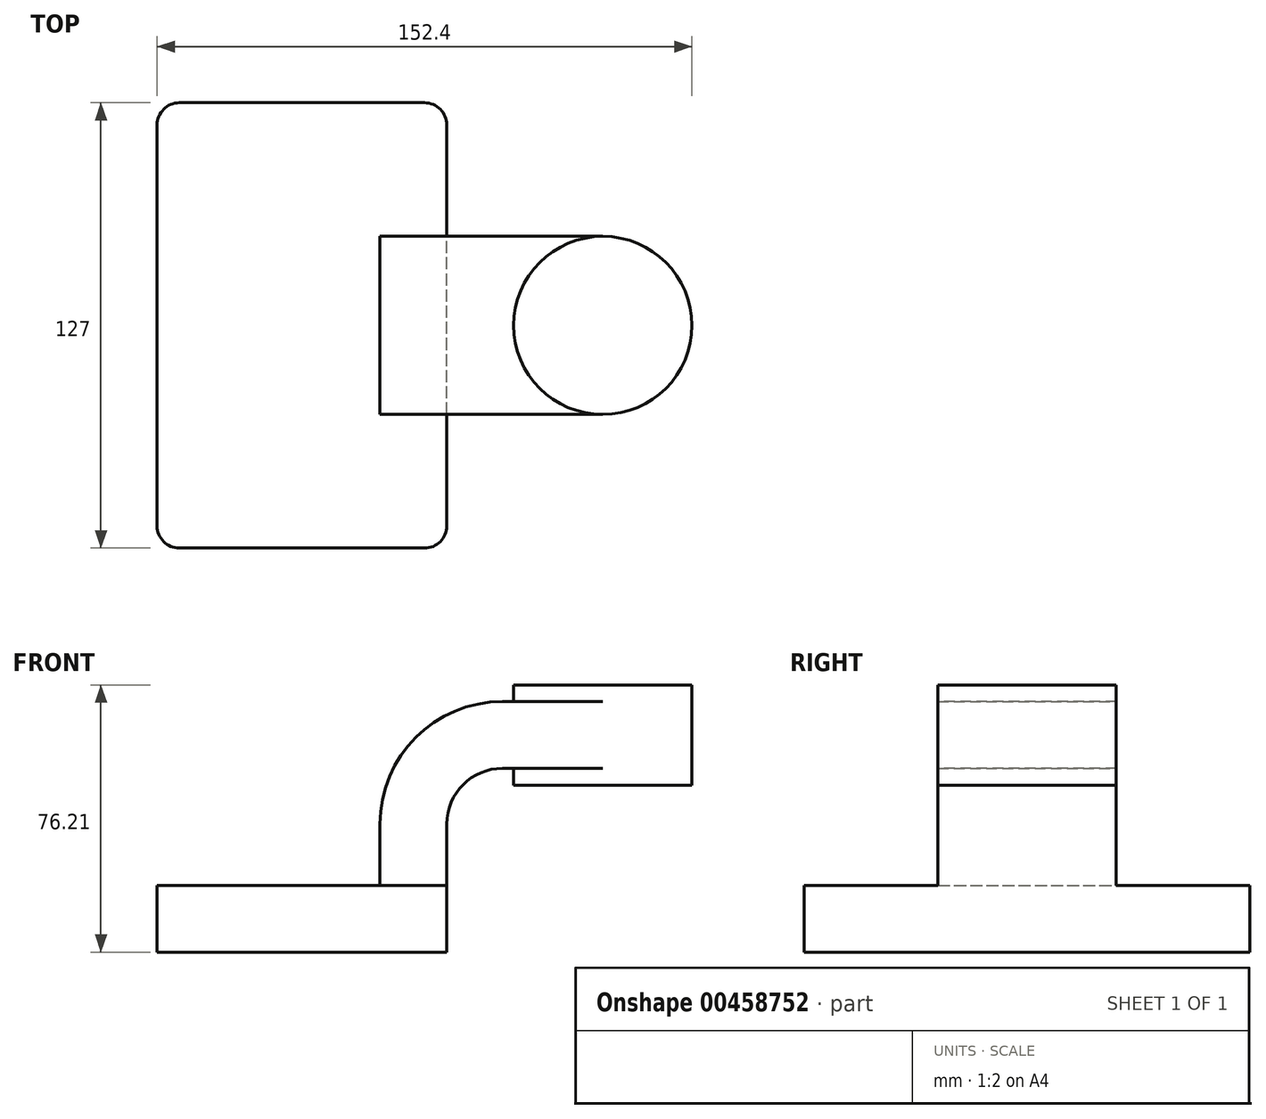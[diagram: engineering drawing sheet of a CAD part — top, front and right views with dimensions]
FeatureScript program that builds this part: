
annotation { "Feature Type Name" : "Feature", "Feature Type Description" : "" }
export const myFeature = defineFeature(function(context is Context, id is Id, definition is map)
    precondition{}
    {
        {
            var Q0;
            Q0=qCreatedBy(makeId("Front.planeOp"),FACE);
            var sketch = newSketch(context, id + "F0", { "sketchPlane" : qUnion([Q0])});
            skLineSegment(sketch, "E0.bottom", {"start": v(41.28, -9.52) * mm, "end": v(-41.28, -9.53) * mm});
            skLineSegment(sketch, "E0.top", {"start": v(41.28, 9.53) * mm, "end": v(-41.28, 9.52) * mm});
            skLineSegment(sketch, "E0.left", {"start": v(41.28, -9.52) * mm, "end": v(41.28, 9.53) * mm});
            skLineSegment(sketch, "E0.right", {"start": v(-41.28, -9.53) * mm, "end": v(-41.28, 9.52) * mm});
            skPoint(sketch, "E0.middle", {"position": v(0, 0) * mm});
            skLineSegment(sketch, "E1.bottom", {"start": v(111.12, 38.1) * mm, "end": v(60.32, 38.1) * mm});
            skLineSegment(sketch, "E1.top", {"start": v(111.12, 66.68) * mm, "end": v(60.32, 66.68) * mm});
            skLineSegment(sketch, "E1.left", {"start": v(111.12, 38.1) * mm, "end": v(111.12, 66.68) * mm});
            skLineSegment(sketch, "E1.right", {"start": v(60.32, 38.1) * mm, "end": v(60.32, 66.68) * mm});
            skPoint(sketch, "E1.middle", {"position": v(85.72, 52.39) * mm});
            skLineSegment(sketch, "E2", {"start": v(41.28, 9.53) * mm, "end": v(41.28, 27) * mm});
            skArc(sketch, "E3", {"start": v(41.28, 27) * mm, "mid": v(45.92, 38.23) * mm, "end": v(57.15, 42.88) * mm});
            skLineSegment(sketch, "E4", {"start": v(57.15, 42.88) * mm, "end": v(85.72, 42.88) * mm});
            skLineSegment(sketch, "E5.0", {"start": v(57.15, 61.93) * mm, "end": v(85.72, 61.93) * mm});
            skArc(sketch, "E5.1", {"start": v(22.23, 27) * mm, "mid": v(32.45, 51.7) * mm, "end": v(57.15, 61.93) * mm});
            skLineSegment(sketch, "E5.2", {"start": v(22.23, 9.53) * mm, "end": v(22.23, 27) * mm});
            skFitSpline(sketch, "E6", {"points": [v(-41.28, 9.52) * mm, v(57.15, 61.93) * mm], "startDerivative": vector(-5.75, 89.36) * mm, "endDerivative": vector(123.9, -8.8) * mm});
            skLineSegment(sketch, "E7", {"start": v(85.72, 66.68) * mm, "end": v(85.72, 38.1) * mm});
            skSolve(sketch);
        }
        {
            var Q0;
            Q0=makeQuery(id+"F0.imprint","IMPRINT",FACE,{"disambiguationData":[TD([[makeQuery(id+"F0.imprint","IMPRINT",EDGE,{"derivedFrom":sQuery(id+"F0.wireOp",EDGE,"E0.bottom")}),-1.0]])]});
            extrude(context, id + "F1", {"entities" : qUnion([Q0]), "depth" : 127 * mm, "symmetric" : true});
        }
        {
            var Q0;
            {var subQ1=sQuery(id+"F0.wireOp",EDGE,"E2");Q0=makeQuery(id+"F0.imprint","IMPRINT",FACE,{"disambiguationData":[TD([[makeQuery(id+"F0.imprint","IMPRINT",EDGE,{"derivedFrom":subQ1}),1.0]])]});}
            var Q1;
            {var subQ0=sQuery(id+"F0.wireOp",EDGE,"E4");var subQ1=sQuery(id+"F0.wireOp",EDGE,"E1.right");var subQ2=makeQuery(id+"F0.imprint","INTERSECT",VERTEX,{"derivedFrom":[subQ1,subQ0]});Q1=makeQuery(id+"F0.imprint","IMPRINT",FACE,{"disambiguationData":[TD([[makeQuery(id+"F0.imprint","IMPRINT",EDGE,{"disambiguationData":[TD([[subQ2,-1.0]])],"derivedFrom":subQ1}),-1.0]])]});}
            extrude(context, id + "F2", {"entities" : qUnion([Q0, Q1]), "operationType" : NewBodyOperationType.ADD, "depth" : 50.8 * mm, "symmetric" : true});
        }
        {
            var Q0;
            Q0=makeQuery(id+"F0.imprint","IMPRINT",FACE,{"disambiguationData":[TD([[makeQuery(id+"F0.imprint","IMPRINT",EDGE,{"derivedFrom":sQuery(id+"F0.wireOp",EDGE,"E5.1")}),1.0]])]});
            extrude(context, id + "F3", {"entities" : qUnion([Q0]), "operationType" : NewBodyOperationType.ADD, "depth" : 15.88 * mm, "symmetric" : true});
        }
        {
            var Q0;
            {var subQ0=sQuery(id+"F0.wireOp",EDGE,"E1.left");Q0=makeQuery(id+"F0.imprint","IMPRINT",FACE,{"disambiguationData":[TD([[makeQuery(id+"F0.imprint","IMPRINT",EDGE,{"derivedFrom":subQ0}),1.0]])]});}
            var Q1;
            Q1=sQuery(id+"F0.wireOp",EDGE,"E7");
            revolve(context, id + "F4", {"operationType" : NewBodyOperationType.ADD, "entities" : qUnion([Q0]), "axis" : qUnion([Q1]), "revolveType" : RevolveType.FULL});
        }
        {
            var Q0;
            Q0=makeQuery(id+"F1.opExtrude","CAP_EDGE",EDGE,{"disambiguationData":[OSD([sQuery(id+"F0.wireOp",EDGE,"E0.left")])],"isStart":false});
            var Q1;
            Q1=makeQuery(id+"F1.opExtrude","CAP_EDGE",EDGE,{"disambiguationData":[OSD([sQuery(id+"F0.wireOp",EDGE,"E0.right")])],"isStart":false});
            var Q2;
            Q2=makeQuery(id+"F1.opExtrude","CAP_EDGE",EDGE,{"disambiguationData":[OSD([sQuery(id+"F0.wireOp",EDGE,"E0.left")])],"isStart":true});
            var Q3;
            Q3=makeQuery(id+"F1.opExtrude","CAP_EDGE",EDGE,{"disambiguationData":[OSD([sQuery(id+"F0.wireOp",EDGE,"E0.right")])],"isStart":true});
            fillet(context, id + "F5", {"entities" : qUnion([Q0, Q1, Q2, Q3]), "radius" : 6.35 * mm, "tangentPropagation" : true, "allowEdgeOverflow" : false});
        }
    });
